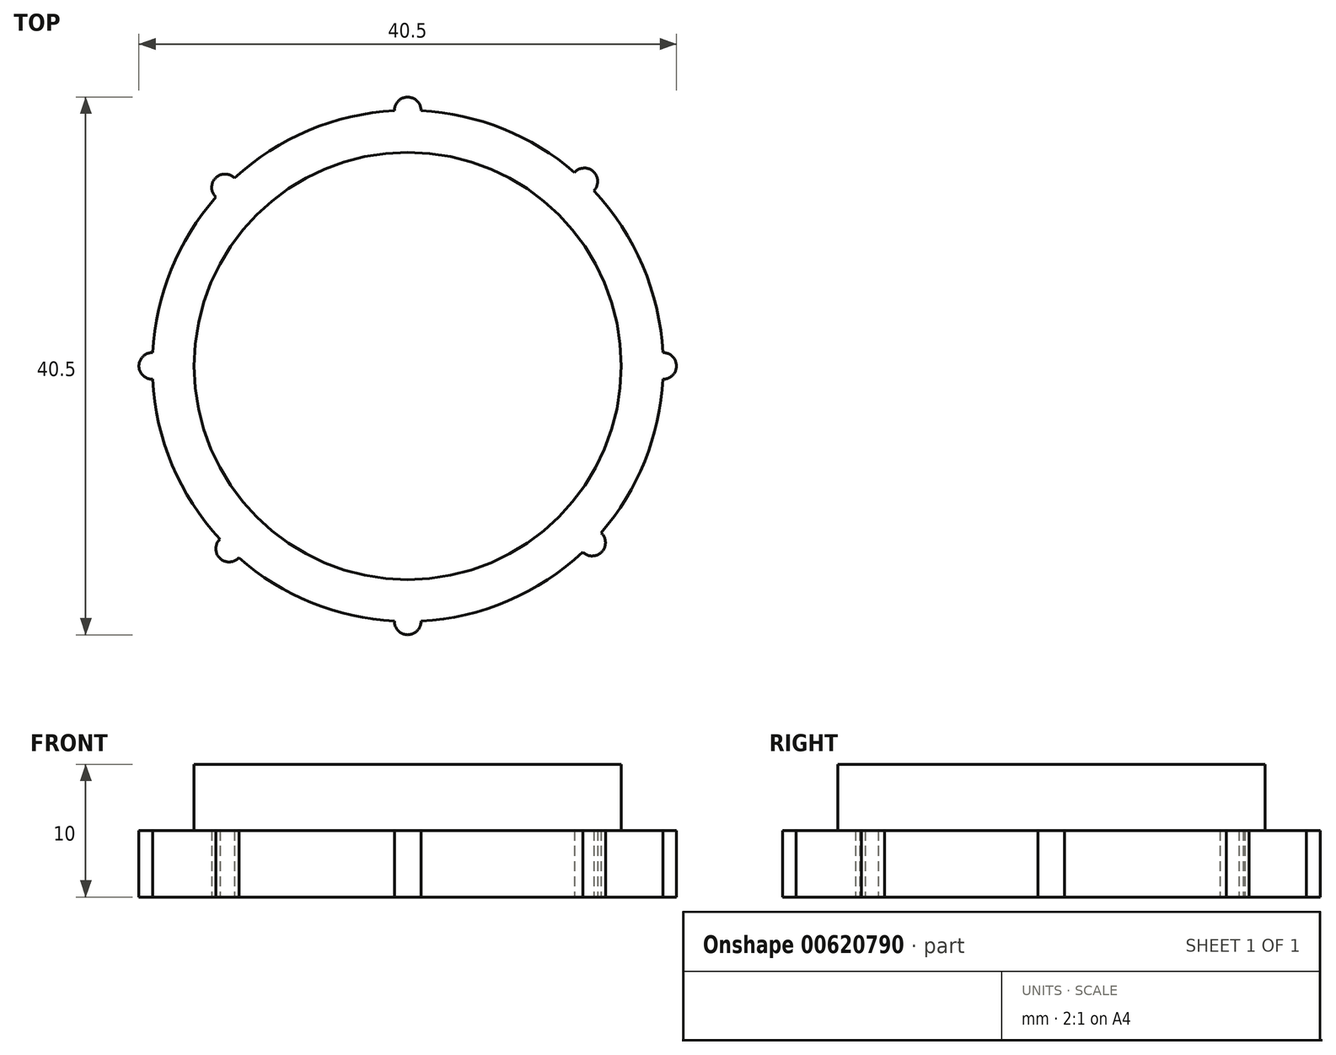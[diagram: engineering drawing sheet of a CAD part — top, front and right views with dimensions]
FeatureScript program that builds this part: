
annotation { "Feature Type Name" : "Feature", "Feature Type Description" : "" }
export const myFeature = defineFeature(function(context is Context, id is Id, definition is map)
    precondition{}
    {
        {
            var Q0;
            Q0=qCreatedBy(makeId("Top.planeOp"),FACE);
            var sketch = newSketch(context, id + "F0", { "sketchPlane" : qUnion([Q0])});
            skCircle(sketch, "E0", {"center": v(0, 0) * mm, "radius": 19.25 * mm});
            skLineSegment(sketch, "E1", {"start": v(0, 0) * mm, "end": v(0, -21.68) * mm, "construction": true});
            skLineSegment(sketch, "E2", {"start": v(0, -21.68) * mm, "end": v(0, 23.61) * mm, "construction": true});
            skLineSegment(sketch, "E3", {"start": v(-21.19, 0) * mm, "end": v(22.61, 0) * mm, "construction": true});
            skCircle(sketch, "E4", {"center": v(0, 19.25) * mm, "radius": 1 * mm});
            skCircle(sketch, "E5", {"center": v(0, -19.25) * mm, "radius": 1 * mm});
            skCircle(sketch, "E6", {"center": v(-19.25, 0) * mm, "radius": 1 * mm});
            skCircle(sketch, "E7", {"center": v(19.25, 0) * mm, "radius": 1 * mm});
            skLineSegment(sketch, "E8", {"start": v(0, 0) * mm, "end": v(22.61, 23.61) * mm, "construction": true});
            skLineSegment(sketch, "E9", {"start": v(0, 0) * mm, "end": v(-21.19, -21.68) * mm, "construction": true});
            skLineSegment(sketch, "E10", {"start": v(0, 0) * mm, "end": v(-21.19, 20.7) * mm, "construction": true});
            skLineSegment(sketch, "E11", {"start": v(0, 0) * mm, "end": v(19.53, -18.7) * mm, "construction": true});
            skCircle(sketch, "E12", {"center": v(-13.77, 13.45) * mm, "radius": 1 * mm});
            skCircle(sketch, "E13", {"center": v(13.31, 13.9) * mm, "radius": 1 * mm});
            skCircle(sketch, "E14", {"center": v(13.9, -13.31) * mm, "radius": 1 * mm});
            skCircle(sketch, "E15", {"center": v(-13.45, -13.77) * mm, "radius": 1 * mm});
            skSolve(sketch);
        }
        {
            var Q0;
            Q0 = qSketchRegion(id + "F0", true);
            extrude(context, id + "F1", {"entities" : qUnion([Q0]), "depth" : 5 * mm, "offsetDistance" : 25 * mm});
        }
        {
            var Q0;
            Q0=makeQuery(id+"F1.opExtrude","CAP_FACE",FACE,{"disambiguationData":[OSD([sQuery(id+"F0.wireOp",EDGE,"E0")])],"isStart":false});
            var sketch = newSketch(context, id + "F2", { "sketchPlane" : qUnion([Q0])});
            skCircle(sketch, "E16", {"center": v(0, 0) * mm, "radius": 16.1 * mm});
            skSolve(sketch);
        }
        {
            var Q0;
            Q0 = qSketchRegion(id + "F2", true);
            extrude(context, id + "F3", {"entities" : qUnion([Q0]), "operationType" : NewBodyOperationType.ADD, "depth" : 5 * mm, "offsetDistance" : 25 * mm});
        }
    });
